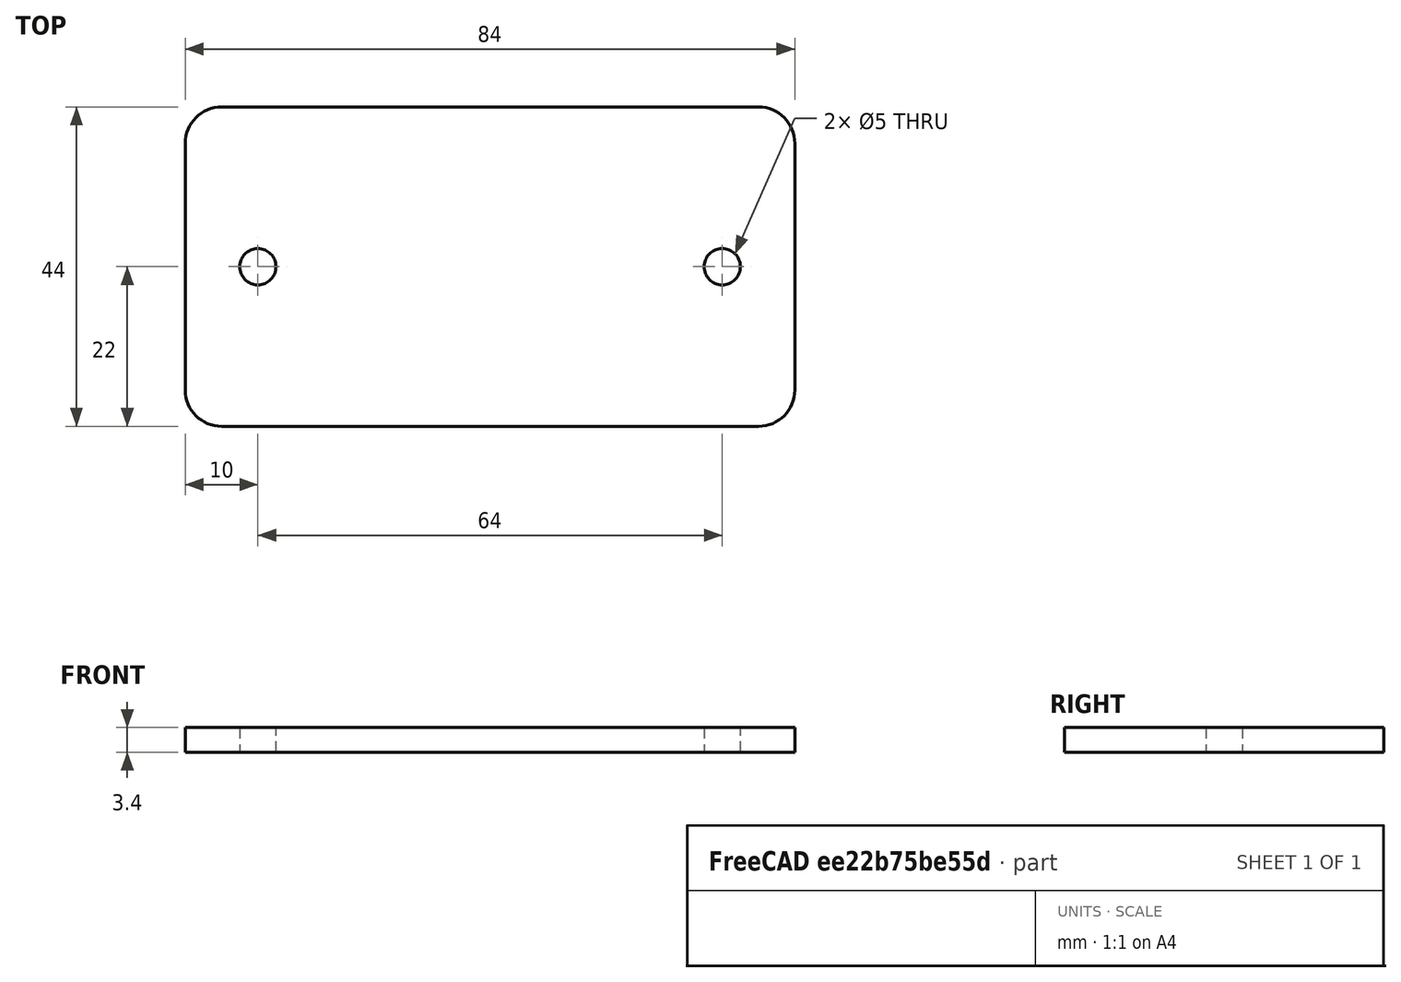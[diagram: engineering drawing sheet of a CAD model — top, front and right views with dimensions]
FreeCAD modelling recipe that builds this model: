
FCSTD DOCUMENT  (FreeCAD 1.0R39109 (Git))
Label: VR lighthouse backplate
License: All rights reserved
LicenseURL: https://en.wikipedia.org/wiki/All_rights_reserved
objects: Sketcher::SketchObject×1, PartDesign::Pad×1, PartDesign::Body×1
note: 6 computed .brp shape members not serialized (recipe doc carries the construction recipe); baked Part::Feature solids carry a one-line shape summary decoded from their .brp

FEATURE [Sketcher::SketchObject] Sketch
  ArcFitTolerance = 1e-06
  AttachmentSupport = -> [XY_Plane]
  FullyConstrained = true
  MakeInternals = false
  MapMode = 5
  sketch-geometry (15):
    g0: LineSegment StartX=-42 StartY=17 StartZ=0 EndX=-42 EndY=-17 EndZ=0
    g1: LineSegment StartX=-37 StartY=-22 StartZ=0 EndX=37 EndY=-22 EndZ=0
    g2: LineSegment StartX=42 StartY=-17 StartZ=0 EndX=42 EndY=17 EndZ=0
    g3: LineSegment StartX=37 StartY=22 StartZ=0 EndX=-37 EndY=22 EndZ=0
    g4: GeomPoint [constr] X=0 Y=0 Z=0
    g5: Circle CenterX=-32 CenterY=0 CenterZ=0 NormalX=0 NormalY=0 NormalZ=1 AngleXU=0 Radius=2.5
    g6: Circle CenterX=32 CenterY=0 CenterZ=0 NormalX=0 NormalY=0 NormalZ=1 AngleXU=0 Radius=2.5
    g7: ArcOfCircle CenterX=-37 CenterY=17 CenterZ=0 NormalX=0 NormalY=0 NormalZ=1 AngleXU=0 Radius=5 StartAngle=1.5708 EndAngle=3.14159
    g8: GeomPoint [constr] X=-42 Y=22 Z=0
    g9: ArcOfCircle CenterX=-37 CenterY=-17 CenterZ=0 NormalX=0 NormalY=0 NormalZ=1 AngleXU=0 Radius=5 StartAngle=3.14159 EndAngle=4.71239
    g10: GeomPoint [constr] X=-42 Y=-22 Z=0
    g11: ArcOfCircle CenterX=37 CenterY=-17 CenterZ=0 NormalX=0 NormalY=0 NormalZ=1 AngleXU=0 Radius=5 StartAngle=4.71239 EndAngle=6.28319
    g12: GeomPoint [constr] X=42 Y=-22 Z=0
    g13: ArcOfCircle CenterX=37 CenterY=17 CenterZ=0 NormalX=0 NormalY=0 NormalZ=1 AngleXU=0 Radius=5 StartAngle=-7.1019e-12 EndAngle=1.5708
    g14: GeomPoint [constr] X=42 Y=22 Z=0
  constraints (33):
    c: Vertical(g0)
    c: Vertical(g2)
    c: Horizontal(g1)
    c: Horizontal(g3)
    c: Symmetric(g12,g8,g4)
    c: Coincident(g4,g-1)
    c: PointOnObject(g5,g-1)
    c: Equal(g6,g5)
    c: Diameter(g5) = 5
    c: DistanceX(g5,g6) = 64
    c: DistanceX(g8,g14) = 84
    c: Symmetric(g5,g6,g4)
    c: DistanceY(g10,g8) = 44
    c: PointOnObject(g8,g3)
    c: PointOnObject(g8,g0)
    c: Tangent(g3,g7) = -1.5708
    c: Tangent(g0,g7) = -1.5708
    c: PointOnObject(g10,g0)
    c: PointOnObject(g10,g1)
    c: Tangent(g0,g9) = -1.5708
    c: Tangent(g1,g9) = -1.5708
    c: PointOnObject(g12,g1)
    c: PointOnObject(g12,g2)
    c: Tangent(g1,g11) = -1.5708
    c: Tangent(g2,g11) = -1.5708
    c: PointOnObject(g14,g3)
    c: PointOnObject(g14,g2)
    c: Tangent(g3,g13) = -1.5708
    c: Tangent(g2,g13) = -1.5708
    c: Equal(g13,g11)
    c: Equal(g11,g9)
    c: Equal(g9,g7)
    c: Diameter(g7) = 10
FEATURE [PartDesign::Pad] Pad
  Direction = (0,0,1)
  Length = 3.4
  Length2 = 10
  Profile = -> Sketch
  ReferenceAxis = -> Sketch [N_Axis]
  Refine = true
  Suppressed = false
  Type = 0
FEATURE [PartDesign::Body] Body
  AllowCompound = false
  Group = -> [Sketch,Pad]
  Origin = -> Origin
  Tip = -> Pad
